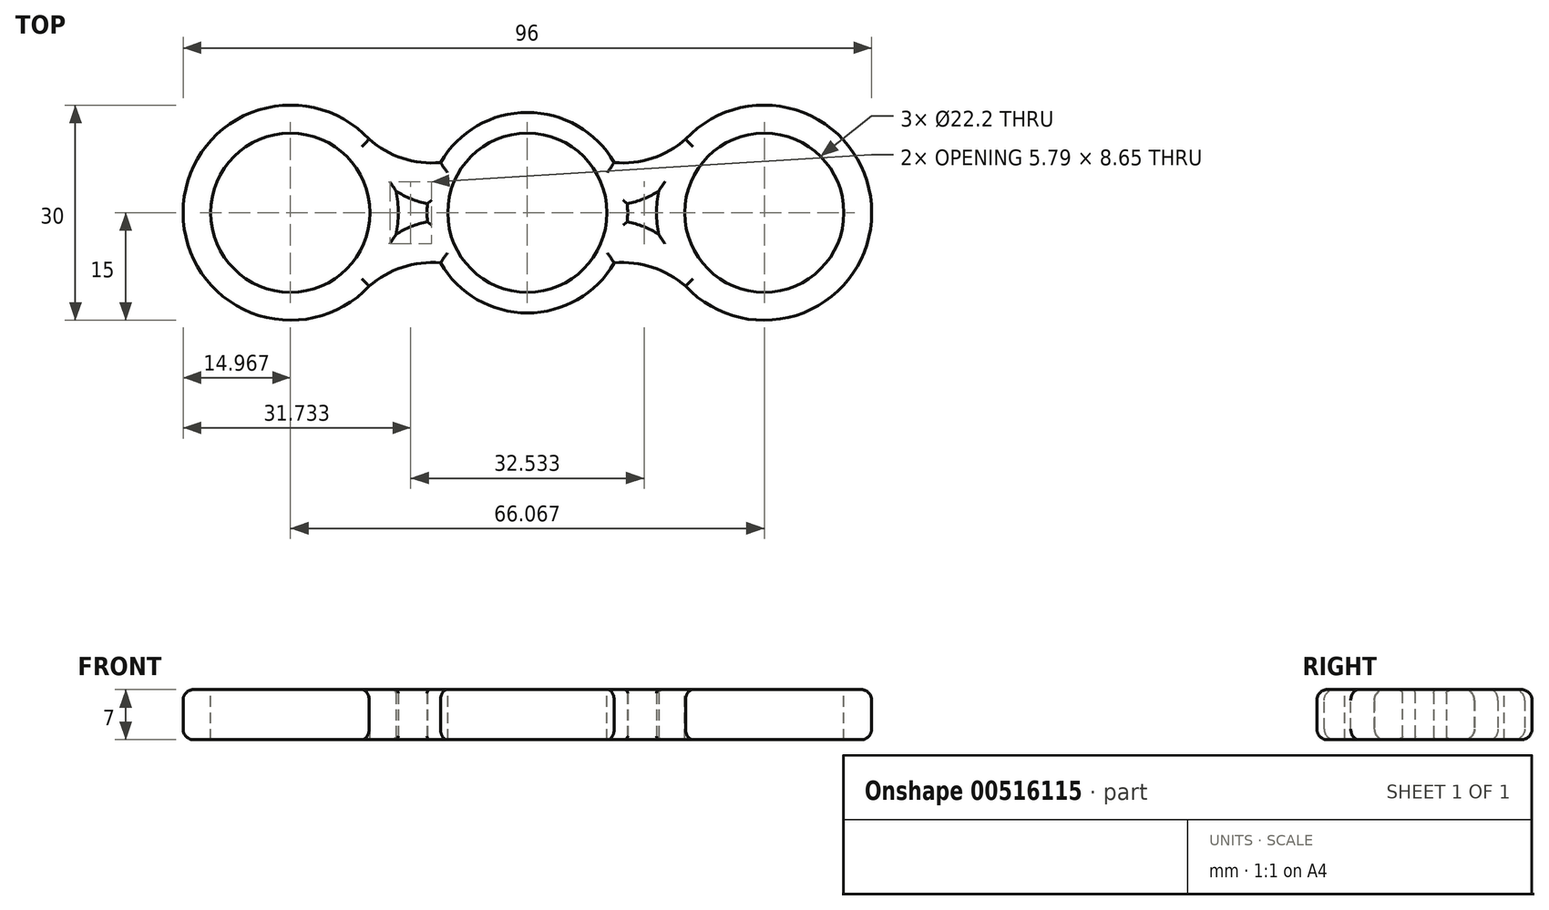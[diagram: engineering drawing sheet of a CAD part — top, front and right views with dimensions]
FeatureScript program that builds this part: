
annotation { "Feature Type Name" : "Feature", "Feature Type Description" : "" }
export const myFeature = defineFeature(function(context is Context, id is Id, definition is map)
    precondition{}
    {
        {
            var Q0;
            Q0=qCreatedBy(makeId("Top.planeOp"),FACE);
            var sketch = newSketch(context, id + "F0", { "sketchPlane" : qUnion([Q0])});
            skLineSegment(sketch, "E0", {"start": v(0, 0) * mm, "end": v(-13.98, 0) * mm});
            skLineSegment(sketch, "E1", {"start": v(0, 0) * mm, "end": v(0, 14) * mm});
            skArc(sketch, "E2", {"start": v(0, 13.98) * mm, "mid": v(-9.89, 9.89) * mm, "end": v(-13.98, 0) * mm});
            skArc(sketch, "E3", {"start": v(-18, 0) * mm, "mid": v(-33, 15) * mm, "end": v(-48, 0) * mm});
            skArc(sketch, "E4", {"start": v(-23, 11.18) * mm, "mid": v(-18.04, 7.82) * mm, "end": v(-12.1, 7) * mm});
            skArc(sketch, "E5", {"start": v(-18.31, 3.04) * mm, "mid": v(-16.2, 1.93) * mm, "end": v(-13.92, 1.28) * mm});
            skLineSegment(sketch, "E6.trimOffspring", {"start": v(-18, 0) * mm, "end": v(-48, 0) * mm});
            skSolve(sketch);
        }
        {
            var Q0;
            Q0 = qSketchRegion(id + "F0", true);
            extrude(context, id + "F1", {"entities" : qUnion([Q0]), "depth" : 7 * mm, "offsetDistance" : 25 * mm});
        }
        {
            var Q0;
            Q0=qCreatedBy(makeId("Top.planeOp"),FACE);
            cPlane(context, id + "F2", {"entities" : qUnion([Q0]), "cplaneType" : CPlaneType.OFFSET, "offset" : 7 * mm, "width" : 150 * mm, "height" : 150 * mm});
        }
        {
            var Q0;
            Q0=qCreatedBy(id+"F2.planeOp",FACE);
            var sketch = newSketch(context, id + "F3", { "sketchPlane" : qUnion([Q0])});
            skCircle(sketch, "E7", {"center": v(-33.03, 0) * mm, "radius": 11.1 * mm});
            skCircle(sketch, "E8", {"center": v(0, 0) * mm, "radius": 11.1 * mm});
            skSolve(sketch);
        }
        {
            var Q0;
            Q0 = qSketchRegion(id + "F3", true);
            extrude(context, id + "F4", {"entities" : qUnion([Q0]), "operationType" : NewBodyOperationType.REMOVE, "oppositeDirection" : true, "depth" : 25 * mm, "offsetDistance" : 25 * mm});
        }
        {
            var Q0;
            Q0=makeQuery(id+"F1.opExtrude","SWEPT_BODY",BODY,{"disambiguationData":[OSD([sQuery(id+"F0.wireOp",EDGE,"E0"),sQuery(id+"F0.wireOp",EDGE,"E1"),sQuery(id+"F0.wireOp",EDGE,"E2"),sQuery(id+"F0.wireOp",EDGE,"E3"),sQuery(id+"F0.wireOp",EDGE,"E4"),sQuery(id+"F0.wireOp",EDGE,"E5"),sQuery(id+"F0.wireOp",EDGE,"E6.trimOffspring")])]});
            transform(context, id + "F5", {"entities" : qUnion([Q0]), "transformType" : TransformType.TRANSLATION_3D, "dx" : 53.6 * mm, "dy" : 0.3 * mm, "dz" : 0 * mm, "makeCopy" : true});
        }
        {
            var Q0;
            Q0=makeQuery(id+"F1.opExtrude","SWEPT_BODY",BODY,{"disambiguationData":[OSD([sQuery(id+"F0.wireOp",EDGE,"E0"),sQuery(id+"F0.wireOp",EDGE,"E1"),sQuery(id+"F0.wireOp",EDGE,"E2"),sQuery(id+"F0.wireOp",EDGE,"E3"),sQuery(id+"F0.wireOp",EDGE,"E4"),sQuery(id+"F0.wireOp",EDGE,"E5"),sQuery(id+"F0.wireOp",EDGE,"E6.trimOffspring")])]});
            var Q1;
            Q1=sQuery(id+"F0.wireOp",EDGE,"E6.trimOffspring");
            transform(context, id + "F6", {"entities" : qUnion([Q0]), "transformType" : TransformType.ROTATION, "transformAxis" : qUnion([Q1]), "angle" : 180 * degree, "makeCopy" : true});
        }
        {
            var Q0;
            Q0=makeQuery(id+"F5.opPattern","COPY",BODY,{"derivedFrom":makeQuery(id+"F1.opExtrude","SWEPT_BODY",BODY,{"disambiguationData":[OSD([sQuery(id+"F0.wireOp",EDGE,"E0"),sQuery(id+"F0.wireOp",EDGE,"E1"),sQuery(id+"F0.wireOp",EDGE,"E2"),sQuery(id+"F0.wireOp",EDGE,"E3"),sQuery(id+"F0.wireOp",EDGE,"E4"),sQuery(id+"F0.wireOp",EDGE,"E5"),sQuery(id+"F0.wireOp",EDGE,"E6.trimOffspring")])]}),"instanceName":"1"});
            deleteBodies(context, id + "F7", {"entities" : qUnion([Q0])});
        }
        {
            var Q0;
            Q0=makeQuery(id+"F6.opPattern","COPY",BODY,{"derivedFrom":makeQuery(id+"F1.opExtrude","SWEPT_BODY",BODY,{"disambiguationData":[OSD([sQuery(id+"F0.wireOp",EDGE,"E0"),sQuery(id+"F0.wireOp",EDGE,"E1"),sQuery(id+"F0.wireOp",EDGE,"E2"),sQuery(id+"F0.wireOp",EDGE,"E3"),sQuery(id+"F0.wireOp",EDGE,"E4"),sQuery(id+"F0.wireOp",EDGE,"E5"),sQuery(id+"F0.wireOp",EDGE,"E6.trimOffspring")])]}),"instanceName":"1"});
            var Q1;
            Q1=qCreatedBy(id+"F2.planeOp",FACE);
            transform(context, id + "F8", {"entities" : qUnion([Q0]), "transformType" : TransformType.TRANSLATION_DISTANCE, "transformDirection" : qUnion([Q1]), "distance" : 7 * mm, "makeCopy" : false});
        }
        {
            var Q0;
            Q0=makeQuery(id+"F1.opExtrude","SWEPT_BODY",BODY,{"disambiguationData":[OSD([sQuery(id+"F0.wireOp",EDGE,"E0"),sQuery(id+"F0.wireOp",EDGE,"E1"),sQuery(id+"F0.wireOp",EDGE,"E2"),sQuery(id+"F0.wireOp",EDGE,"E3"),sQuery(id+"F0.wireOp",EDGE,"E4"),sQuery(id+"F0.wireOp",EDGE,"E5"),sQuery(id+"F0.wireOp",EDGE,"E6.trimOffspring")])]});
            var Q1;
            Q1=makeQuery(id+"F6.opPattern","COPY",BODY,{"derivedFrom":makeQuery(id+"F1.opExtrude","SWEPT_BODY",BODY,{"disambiguationData":[OSD([sQuery(id+"F0.wireOp",EDGE,"E0"),sQuery(id+"F0.wireOp",EDGE,"E1"),sQuery(id+"F0.wireOp",EDGE,"E2"),sQuery(id+"F0.wireOp",EDGE,"E3"),sQuery(id+"F0.wireOp",EDGE,"E4"),sQuery(id+"F0.wireOp",EDGE,"E5"),sQuery(id+"F0.wireOp",EDGE,"E6.trimOffspring")])]}),"instanceName":"1"});
            var Q2;
            Q2=sQuery(id+"F0.wireOp",EDGE,"E1");
            transform(context, id + "F9", {"entities" : qUnion([Q0, Q1]), "transformType" : TransformType.ROTATION, "transformAxis" : qUnion([Q2]), "angle" : 180 * degree, "makeCopy" : true});
        }
        {
            var Q0;
            Q0=makeQuery(id+"F9.opPattern","COPY",BODY,{"derivedFrom":makeQuery(id+"F1.opExtrude","SWEPT_BODY",BODY,{"disambiguationData":[OSD([sQuery(id+"F0.wireOp",EDGE,"E0"),sQuery(id+"F0.wireOp",EDGE,"E1"),sQuery(id+"F0.wireOp",EDGE,"E2"),sQuery(id+"F0.wireOp",EDGE,"E3"),sQuery(id+"F0.wireOp",EDGE,"E4"),sQuery(id+"F0.wireOp",EDGE,"E5"),sQuery(id+"F0.wireOp",EDGE,"E6.trimOffspring")])]}),"instanceName":"1"});
            var Q1;
            Q1=makeQuery(id+"F9.opPattern","COPY",BODY,{"derivedFrom":makeQuery(id+"F6.opPattern","COPY",BODY,{"derivedFrom":makeQuery(id+"F1.opExtrude","SWEPT_BODY",BODY,{"disambiguationData":[OSD([sQuery(id+"F0.wireOp",EDGE,"E0"),sQuery(id+"F0.wireOp",EDGE,"E1"),sQuery(id+"F0.wireOp",EDGE,"E2"),sQuery(id+"F0.wireOp",EDGE,"E3"),sQuery(id+"F0.wireOp",EDGE,"E4"),sQuery(id+"F0.wireOp",EDGE,"E5"),sQuery(id+"F0.wireOp",EDGE,"E6.trimOffspring")])]}),"instanceName":"1"}),"instanceName":"1"});
            var Q2;
            Q2=qCreatedBy(id+"F2.planeOp",FACE);
            transform(context, id + "F10", {"entities" : qUnion([Q0, Q1]), "transformType" : TransformType.TRANSLATION_DISTANCE, "transformDirection" : qUnion([Q2]), "distance" : 7 * mm, "makeCopy" : false});
        }
        {
            var Q0;
            Q0=makeQuery(id+"F1.opExtrude","SWEPT_BODY",BODY,{"disambiguationData":[OSD([sQuery(id+"F0.wireOp",EDGE,"E0"),sQuery(id+"F0.wireOp",EDGE,"E1"),sQuery(id+"F0.wireOp",EDGE,"E2"),sQuery(id+"F0.wireOp",EDGE,"E3"),sQuery(id+"F0.wireOp",EDGE,"E4"),sQuery(id+"F0.wireOp",EDGE,"E5"),sQuery(id+"F0.wireOp",EDGE,"E6.trimOffspring")])]});
            var Q1;
            Q1=makeQuery(id+"F6.opPattern","COPY",BODY,{"derivedFrom":makeQuery(id+"F1.opExtrude","SWEPT_BODY",BODY,{"disambiguationData":[OSD([sQuery(id+"F0.wireOp",EDGE,"E0"),sQuery(id+"F0.wireOp",EDGE,"E1"),sQuery(id+"F0.wireOp",EDGE,"E2"),sQuery(id+"F0.wireOp",EDGE,"E3"),sQuery(id+"F0.wireOp",EDGE,"E4"),sQuery(id+"F0.wireOp",EDGE,"E5"),sQuery(id+"F0.wireOp",EDGE,"E6.trimOffspring")])]}),"instanceName":"1"});
            var Q2;
            Q2=makeQuery(id+"F9.opPattern","COPY",BODY,{"derivedFrom":makeQuery(id+"F6.opPattern","COPY",BODY,{"derivedFrom":makeQuery(id+"F1.opExtrude","SWEPT_BODY",BODY,{"disambiguationData":[OSD([sQuery(id+"F0.wireOp",EDGE,"E0"),sQuery(id+"F0.wireOp",EDGE,"E1"),sQuery(id+"F0.wireOp",EDGE,"E2"),sQuery(id+"F0.wireOp",EDGE,"E3"),sQuery(id+"F0.wireOp",EDGE,"E4"),sQuery(id+"F0.wireOp",EDGE,"E5"),sQuery(id+"F0.wireOp",EDGE,"E6.trimOffspring")])]}),"instanceName":"1"}),"instanceName":"1"});
            var Q3;
            Q3=makeQuery(id+"F9.opPattern","COPY",BODY,{"derivedFrom":makeQuery(id+"F1.opExtrude","SWEPT_BODY",BODY,{"disambiguationData":[OSD([sQuery(id+"F0.wireOp",EDGE,"E0"),sQuery(id+"F0.wireOp",EDGE,"E1"),sQuery(id+"F0.wireOp",EDGE,"E2"),sQuery(id+"F0.wireOp",EDGE,"E3"),sQuery(id+"F0.wireOp",EDGE,"E4"),sQuery(id+"F0.wireOp",EDGE,"E5"),sQuery(id+"F0.wireOp",EDGE,"E6.trimOffspring")])]}),"instanceName":"1"});
            booleanBodies(context, id + "F11", {"operationType" : BooleanOperationType.UNION, "tools" : qUnion([Q0, Q1, Q2, Q3])});
        }
        {
            var Q0;
            {var subQ0=sQuery(id+"F0.wireOp",EDGE,"E3");var subQ1=sQuery(id+"F0.wireOp",EDGE,"E4");var subQ2=makeQuery(id+"F0.imprint","INTERSECT",VERTEX,{"disambiguationData":[OD(0.0)],"derivedFrom":[subQ0,subQ1]});var subQ3=makeQuery(id+"F0.imprint","IMPRINT",EDGE,{"disambiguationData":[TD([[makeQuery(id+"F0.imprint","INTERSECT",VERTEX,{"disambiguationData":[OD(1.0)],"derivedFrom":[subQ0,sQuery(id+"F0.wireOp",EDGE,"E6.trimOffspring")]}),1.0]])],"derivedFrom":subQ0});var subQ4=makeQuery(id+"F0.imprint","IMPRINT",EDGE,{"disambiguationData":[TD([[subQ2,1.0]])],"derivedFrom":subQ0});Q0=makeQuery(id+"F11.opBoolean","MERGE",EDGE,{"derivedFrom":[makeQuery(id+"F9.opPattern","COPY",EDGE,{"derivedFrom":makeQuery(id+"F1.opExtrude","CAP_EDGE",EDGE,{"disambiguationData":[OSD([subQ0]),TDD([subQ4,subQ3])],"isStart":false}),"instanceName":"1"}),makeQuery(id+"F9.opPattern","COPY",EDGE,{"derivedFrom":makeQuery(id+"F6.opPattern","COPY",EDGE,{"derivedFrom":makeQuery(id+"F1.opExtrude","CAP_EDGE",EDGE,{"disambiguationData":[OSD([subQ0]),TDD([subQ4,subQ3])],"isStart":true}),"instanceName":"1"}),"instanceName":"1"})]});}
            var Q1;
            Q1=makeQuery(id+"F9.opPattern","COPY",EDGE,{"derivedFrom":makeQuery(id+"F1.opExtrude","CAP_EDGE",EDGE,{"disambiguationData":[OSD([sQuery(id+"F0.wireOp",EDGE,"E4")])],"isStart":false}),"instanceName":"1"});
            var Q2;
            Q2=makeQuery(id+"F9.opPattern","COPY",EDGE,{"derivedFrom":makeQuery(id+"F6.opPattern","COPY",EDGE,{"derivedFrom":makeQuery(id+"F1.opExtrude","CAP_EDGE",EDGE,{"disambiguationData":[OSD([sQuery(id+"F0.wireOp",EDGE,"E4")])],"isStart":true}),"instanceName":"1"}),"instanceName":"1"});
            var Q3;
            {var subQ0=sQuery(id+"F0.wireOp",EDGE,"E2");var subQ1=makeQuery(id+"F0.imprint","IMPRINT",EDGE,{"disambiguationData":[TD([[makeQuery(id+"F0.imprint","INTERSECT",VERTEX,{"derivedFrom":[sQuery(id+"F0.wireOp",EDGE,"E1"),subQ0]}),-1.0]])],"derivedFrom":subQ0});Q3=makeQuery(id+"F11.opBoolean","MERGE",EDGE,{"derivedFrom":[makeQuery(id+"F6.opPattern","COPY",EDGE,{"derivedFrom":makeQuery(id+"F1.opExtrude","CAP_EDGE",EDGE,{"disambiguationData":[OSD([subQ0]),TDD([subQ1])],"isStart":false}),"instanceName":"1"}),makeQuery(id+"F9.opPattern","COPY",EDGE,{"derivedFrom":makeQuery(id+"F6.opPattern","COPY",EDGE,{"derivedFrom":makeQuery(id+"F1.opExtrude","CAP_EDGE",EDGE,{"disambiguationData":[OSD([subQ0]),TDD([subQ1])],"isStart":true}),"instanceName":"1"}),"instanceName":"1"})]});}
            var Q4;
            {var subQ0=sQuery(id+"F0.wireOp",EDGE,"E2");var subQ1=makeQuery(id+"F0.imprint","IMPRINT",EDGE,{"disambiguationData":[TD([[makeQuery(id+"F0.imprint","INTERSECT",VERTEX,{"derivedFrom":[sQuery(id+"F0.wireOp",EDGE,"E1"),subQ0]}),-1.0]])],"derivedFrom":subQ0});Q4=makeQuery(id+"F11.opBoolean","MERGE",EDGE,{"derivedFrom":[makeQuery(id+"F1.opExtrude","CAP_EDGE",EDGE,{"disambiguationData":[OSD([subQ0]),TDD([subQ1])],"isStart":true}),makeQuery(id+"F9.opPattern","COPY",EDGE,{"derivedFrom":makeQuery(id+"F1.opExtrude","CAP_EDGE",EDGE,{"disambiguationData":[OSD([subQ0]),TDD([subQ1])],"isStart":false}),"instanceName":"1"})]});}
            var Q5;
            Q5=makeQuery(id+"F1.opExtrude","CAP_EDGE",EDGE,{"disambiguationData":[OSD([sQuery(id+"F0.wireOp",EDGE,"E4")])],"isStart":true});
            var Q6;
            {var subQ0=sQuery(id+"F0.wireOp",EDGE,"E3");var subQ1=sQuery(id+"F0.wireOp",EDGE,"E4");var subQ2=makeQuery(id+"F0.imprint","INTERSECT",VERTEX,{"disambiguationData":[OD(0.0)],"derivedFrom":[subQ0,subQ1]});var subQ3=makeQuery(id+"F0.imprint","IMPRINT",EDGE,{"disambiguationData":[TD([[makeQuery(id+"F0.imprint","INTERSECT",VERTEX,{"disambiguationData":[OD(1.0)],"derivedFrom":[subQ0,sQuery(id+"F0.wireOp",EDGE,"E6.trimOffspring")]}),1.0]])],"derivedFrom":subQ0});var subQ4=makeQuery(id+"F0.imprint","IMPRINT",EDGE,{"disambiguationData":[TD([[subQ2,1.0]])],"derivedFrom":subQ0});Q6=makeQuery(id+"F11.opBoolean","MERGE",EDGE,{"derivedFrom":[makeQuery(id+"F1.opExtrude","CAP_EDGE",EDGE,{"disambiguationData":[OSD([subQ0]),TDD([subQ4,subQ3])],"isStart":true}),makeQuery(id+"F6.opPattern","COPY",EDGE,{"derivedFrom":makeQuery(id+"F1.opExtrude","CAP_EDGE",EDGE,{"disambiguationData":[OSD([subQ0]),TDD([subQ4,subQ3])],"isStart":false}),"instanceName":"1"})]});}
            var Q7;
            Q7=makeQuery(id+"F6.opPattern","COPY",EDGE,{"derivedFrom":makeQuery(id+"F1.opExtrude","CAP_EDGE",EDGE,{"disambiguationData":[OSD([sQuery(id+"F0.wireOp",EDGE,"E4")])],"isStart":false}),"instanceName":"1"});
            fillet(context, id + "F12", {"entities" : qUnion([Q0, Q1, Q2, Q3, Q4, Q5, Q6, Q7]), "radius" : 1.5 * mm, "tangentPropagation" : true, "allowEdgeOverflow" : false});
        }
        {
            var Q0;
            {var subQ0=sQuery(id+"F0.wireOp",EDGE,"E3");var subQ1=sQuery(id+"F0.wireOp",EDGE,"E4");var subQ2=makeQuery(id+"F0.imprint","INTERSECT",VERTEX,{"disambiguationData":[OD(0.0)],"derivedFrom":[subQ0,subQ1]});var subQ3=makeQuery(id+"F0.imprint","IMPRINT",EDGE,{"disambiguationData":[TD([[makeQuery(id+"F0.imprint","INTERSECT",VERTEX,{"disambiguationData":[OD(1.0)],"derivedFrom":[subQ0,sQuery(id+"F0.wireOp",EDGE,"E6.trimOffspring")]}),1.0]])],"derivedFrom":subQ0});var subQ4=makeQuery(id+"F0.imprint","IMPRINT",EDGE,{"disambiguationData":[TD([[subQ2,1.0]])],"derivedFrom":subQ0});Q0=makeQuery(id+"F11.opBoolean","MERGE",EDGE,{"derivedFrom":[makeQuery(id+"F1.opExtrude","CAP_EDGE",EDGE,{"disambiguationData":[OSD([subQ0]),TDD([subQ4,subQ3])],"isStart":false}),makeQuery(id+"F6.opPattern","COPY",EDGE,{"derivedFrom":makeQuery(id+"F1.opExtrude","CAP_EDGE",EDGE,{"disambiguationData":[OSD([subQ0]),TDD([subQ4,subQ3])],"isStart":true}),"instanceName":"1"})]});}
            var Q1;
            Q1=makeQuery(id+"F1.opExtrude","CAP_EDGE",EDGE,{"disambiguationData":[OSD([sQuery(id+"F0.wireOp",EDGE,"E4")])],"isStart":false});
            var Q2;
            Q2=makeQuery(id+"F6.opPattern","COPY",EDGE,{"derivedFrom":makeQuery(id+"F1.opExtrude","CAP_EDGE",EDGE,{"disambiguationData":[OSD([sQuery(id+"F0.wireOp",EDGE,"E4")])],"isStart":true}),"instanceName":"1"});
            var Q3;
            {var subQ0=sQuery(id+"F0.wireOp",EDGE,"E2");var subQ1=makeQuery(id+"F0.imprint","IMPRINT",EDGE,{"disambiguationData":[TD([[makeQuery(id+"F0.imprint","INTERSECT",VERTEX,{"derivedFrom":[sQuery(id+"F0.wireOp",EDGE,"E1"),subQ0]}),-1.0]])],"derivedFrom":subQ0});Q3=makeQuery(id+"F11.opBoolean","MERGE",EDGE,{"derivedFrom":[makeQuery(id+"F6.opPattern","COPY",EDGE,{"derivedFrom":makeQuery(id+"F1.opExtrude","CAP_EDGE",EDGE,{"disambiguationData":[OSD([subQ0]),TDD([subQ1])],"isStart":true}),"instanceName":"1"}),makeQuery(id+"F9.opPattern","COPY",EDGE,{"derivedFrom":makeQuery(id+"F6.opPattern","COPY",EDGE,{"derivedFrom":makeQuery(id+"F1.opExtrude","CAP_EDGE",EDGE,{"disambiguationData":[OSD([subQ0]),TDD([subQ1])],"isStart":false}),"instanceName":"1"}),"instanceName":"1"})]});}
            var Q4;
            {var subQ0=sQuery(id+"F0.wireOp",EDGE,"E2");var subQ1=makeQuery(id+"F0.imprint","IMPRINT",EDGE,{"disambiguationData":[TD([[makeQuery(id+"F0.imprint","INTERSECT",VERTEX,{"derivedFrom":[sQuery(id+"F0.wireOp",EDGE,"E1"),subQ0]}),-1.0]])],"derivedFrom":subQ0});Q4=makeQuery(id+"F11.opBoolean","MERGE",EDGE,{"derivedFrom":[makeQuery(id+"F1.opExtrude","CAP_EDGE",EDGE,{"disambiguationData":[OSD([subQ0]),TDD([subQ1])],"isStart":false}),makeQuery(id+"F9.opPattern","COPY",EDGE,{"derivedFrom":makeQuery(id+"F1.opExtrude","CAP_EDGE",EDGE,{"disambiguationData":[OSD([subQ0]),TDD([subQ1])],"isStart":true}),"instanceName":"1"})]});}
            var Q5;
            Q5=makeQuery(id+"F9.opPattern","COPY",EDGE,{"derivedFrom":makeQuery(id+"F1.opExtrude","CAP_EDGE",EDGE,{"disambiguationData":[OSD([sQuery(id+"F0.wireOp",EDGE,"E4")])],"isStart":true}),"instanceName":"1"});
            var Q6;
            {var subQ0=sQuery(id+"F0.wireOp",EDGE,"E3");var subQ1=sQuery(id+"F0.wireOp",EDGE,"E4");var subQ2=makeQuery(id+"F0.imprint","INTERSECT",VERTEX,{"disambiguationData":[OD(0.0)],"derivedFrom":[subQ0,subQ1]});var subQ3=makeQuery(id+"F0.imprint","IMPRINT",EDGE,{"disambiguationData":[TD([[makeQuery(id+"F0.imprint","INTERSECT",VERTEX,{"disambiguationData":[OD(1.0)],"derivedFrom":[subQ0,sQuery(id+"F0.wireOp",EDGE,"E6.trimOffspring")]}),1.0]])],"derivedFrom":subQ0});var subQ4=makeQuery(id+"F0.imprint","IMPRINT",EDGE,{"disambiguationData":[TD([[subQ2,1.0]])],"derivedFrom":subQ0});Q6=makeQuery(id+"F11.opBoolean","MERGE",EDGE,{"derivedFrom":[makeQuery(id+"F9.opPattern","COPY",EDGE,{"derivedFrom":makeQuery(id+"F1.opExtrude","CAP_EDGE",EDGE,{"disambiguationData":[OSD([subQ0]),TDD([subQ4,subQ3])],"isStart":true}),"instanceName":"1"}),makeQuery(id+"F9.opPattern","COPY",EDGE,{"derivedFrom":makeQuery(id+"F6.opPattern","COPY",EDGE,{"derivedFrom":makeQuery(id+"F1.opExtrude","CAP_EDGE",EDGE,{"disambiguationData":[OSD([subQ0]),TDD([subQ4,subQ3])],"isStart":false}),"instanceName":"1"}),"instanceName":"1"})]});}
            var Q7;
            Q7=makeQuery(id+"F9.opPattern","COPY",EDGE,{"derivedFrom":makeQuery(id+"F6.opPattern","COPY",EDGE,{"derivedFrom":makeQuery(id+"F1.opExtrude","CAP_EDGE",EDGE,{"disambiguationData":[OSD([sQuery(id+"F0.wireOp",EDGE,"E4")])],"isStart":false}),"instanceName":"1"}),"instanceName":"1"});
            fillet(context, id + "F13", {"entities" : qUnion([Q0, Q1, Q2, Q3, Q4, Q5, Q6, Q7]), "radius" : 1.5 * mm, "tangentPropagation" : true, "allowEdgeOverflow" : false});
        }
        {
            var Q0;
            Q0=makeQuery(id+"F9.opPattern","COPY",EDGE,{"derivedFrom":makeQuery(id+"F1.opExtrude","CAP_EDGE",EDGE,{"disambiguationData":[OSD([sQuery(id+"F0.wireOp",EDGE,"E5")])],"isStart":false}),"instanceName":"1"});
            var Q1;
            Q1=makeQuery(id+"F1.opExtrude","CAP_EDGE",EDGE,{"disambiguationData":[OSD([sQuery(id+"F0.wireOp",EDGE,"E5")])],"isStart":true});
            var Q2;
            {var subQ0=sQuery(id+"F0.wireOp",EDGE,"E3");var subQ1=makeQuery(id+"F0.imprint","IMPRINT",EDGE,{"disambiguationData":[TD([[makeQuery(id+"F0.imprint","INTERSECT",VERTEX,{"disambiguationData":[OD(0.0)],"derivedFrom":[subQ0,sQuery(id+"F0.wireOp",EDGE,"E6.trimOffspring")]}),-1.0]])],"derivedFrom":subQ0});Q2=makeQuery(id+"F11.opBoolean","MERGE",EDGE,{"derivedFrom":[makeQuery(id+"F1.opExtrude","CAP_EDGE",EDGE,{"disambiguationData":[OSD([subQ0]),TDD([subQ1])],"isStart":true}),makeQuery(id+"F6.opPattern","COPY",EDGE,{"derivedFrom":makeQuery(id+"F1.opExtrude","CAP_EDGE",EDGE,{"disambiguationData":[OSD([subQ0]),TDD([subQ1])],"isStart":false}),"instanceName":"1"})]});}
            var Q3;
            Q3=makeQuery(id+"F6.opPattern","COPY",EDGE,{"derivedFrom":makeQuery(id+"F1.opExtrude","CAP_EDGE",EDGE,{"disambiguationData":[OSD([sQuery(id+"F0.wireOp",EDGE,"E5")])],"isStart":false}),"instanceName":"1"});
            var Q4;
            {var subQ0=sQuery(id+"F0.wireOp",EDGE,"E3");var subQ1=makeQuery(id+"F0.imprint","IMPRINT",EDGE,{"disambiguationData":[TD([[makeQuery(id+"F0.imprint","INTERSECT",VERTEX,{"disambiguationData":[OD(0.0)],"derivedFrom":[subQ0,sQuery(id+"F0.wireOp",EDGE,"E6.trimOffspring")]}),-1.0]])],"derivedFrom":subQ0});Q4=makeQuery(id+"F11.opBoolean","MERGE",EDGE,{"derivedFrom":[makeQuery(id+"F1.opExtrude","CAP_EDGE",EDGE,{"disambiguationData":[OSD([subQ0]),TDD([subQ1])],"isStart":false}),makeQuery(id+"F6.opPattern","COPY",EDGE,{"derivedFrom":makeQuery(id+"F1.opExtrude","CAP_EDGE",EDGE,{"disambiguationData":[OSD([subQ0]),TDD([subQ1])],"isStart":true}),"instanceName":"1"})]});}
            var Q5;
            Q5=makeQuery(id+"F1.opExtrude","CAP_EDGE",EDGE,{"disambiguationData":[OSD([sQuery(id+"F0.wireOp",EDGE,"E5")])],"isStart":false});
            var Q6;
            {var subQ0=sQuery(id+"F0.wireOp",EDGE,"E2");var subQ1=makeQuery(id+"F0.imprint","IMPRINT",EDGE,{"disambiguationData":[TD([[makeQuery(id+"F0.imprint","INTERSECT",VERTEX,{"derivedFrom":[sQuery(id+"F0.wireOp",EDGE,"E0"),subQ0]}),1.0]])],"derivedFrom":subQ0});Q6=makeQuery(id+"F11.opBoolean","MERGE",EDGE,{"derivedFrom":[makeQuery(id+"F1.opExtrude","CAP_EDGE",EDGE,{"disambiguationData":[OSD([subQ0]),TDD([subQ1])],"isStart":false}),makeQuery(id+"F6.opPattern","COPY",EDGE,{"derivedFrom":makeQuery(id+"F1.opExtrude","CAP_EDGE",EDGE,{"disambiguationData":[OSD([subQ0]),TDD([subQ1])],"isStart":true}),"instanceName":"1"})]});}
            var Q7;
            Q7=makeQuery(id+"F6.opPattern","COPY",EDGE,{"derivedFrom":makeQuery(id+"F1.opExtrude","CAP_EDGE",EDGE,{"disambiguationData":[OSD([sQuery(id+"F0.wireOp",EDGE,"E5")])],"isStart":true}),"instanceName":"1"});
            var Q8;
            {var subQ0=sQuery(id+"F0.wireOp",EDGE,"E2");var subQ1=makeQuery(id+"F0.imprint","IMPRINT",EDGE,{"disambiguationData":[TD([[makeQuery(id+"F0.imprint","INTERSECT",VERTEX,{"derivedFrom":[sQuery(id+"F0.wireOp",EDGE,"E0"),subQ0]}),1.0]])],"derivedFrom":subQ0});Q8=makeQuery(id+"F11.opBoolean","MERGE",EDGE,{"derivedFrom":[makeQuery(id+"F1.opExtrude","CAP_EDGE",EDGE,{"disambiguationData":[OSD([subQ0]),TDD([subQ1])],"isStart":true}),makeQuery(id+"F6.opPattern","COPY",EDGE,{"derivedFrom":makeQuery(id+"F1.opExtrude","CAP_EDGE",EDGE,{"disambiguationData":[OSD([subQ0]),TDD([subQ1])],"isStart":false}),"instanceName":"1"})]});}
            var Q9;
            {var subQ0=sQuery(id+"F0.wireOp",EDGE,"E2");var subQ1=makeQuery(id+"F0.imprint","IMPRINT",EDGE,{"disambiguationData":[TD([[makeQuery(id+"F0.imprint","INTERSECT",VERTEX,{"derivedFrom":[sQuery(id+"F0.wireOp",EDGE,"E0"),subQ0]}),1.0]])],"derivedFrom":subQ0});Q9=makeQuery(id+"F11.opBoolean","MERGE",EDGE,{"derivedFrom":[makeQuery(id+"F9.opPattern","COPY",EDGE,{"derivedFrom":makeQuery(id+"F1.opExtrude","CAP_EDGE",EDGE,{"disambiguationData":[OSD([subQ0]),TDD([subQ1])],"isStart":false}),"instanceName":"1"}),makeQuery(id+"F9.opPattern","COPY",EDGE,{"derivedFrom":makeQuery(id+"F6.opPattern","COPY",EDGE,{"derivedFrom":makeQuery(id+"F1.opExtrude","CAP_EDGE",EDGE,{"disambiguationData":[OSD([subQ0]),TDD([subQ1])],"isStart":true}),"instanceName":"1"}),"instanceName":"1"})]});}
            var Q10;
            {var subQ0=sQuery(id+"F0.wireOp",EDGE,"E3");var subQ1=makeQuery(id+"F0.imprint","IMPRINT",EDGE,{"disambiguationData":[TD([[makeQuery(id+"F0.imprint","INTERSECT",VERTEX,{"disambiguationData":[OD(0.0)],"derivedFrom":[subQ0,sQuery(id+"F0.wireOp",EDGE,"E6.trimOffspring")]}),-1.0]])],"derivedFrom":subQ0});Q10=makeQuery(id+"F11.opBoolean","MERGE",EDGE,{"derivedFrom":[makeQuery(id+"F9.opPattern","COPY",EDGE,{"derivedFrom":makeQuery(id+"F1.opExtrude","CAP_EDGE",EDGE,{"disambiguationData":[OSD([subQ0]),TDD([subQ1])],"isStart":false}),"instanceName":"1"}),makeQuery(id+"F9.opPattern","COPY",EDGE,{"derivedFrom":makeQuery(id+"F6.opPattern","COPY",EDGE,{"derivedFrom":makeQuery(id+"F1.opExtrude","CAP_EDGE",EDGE,{"disambiguationData":[OSD([subQ0]),TDD([subQ1])],"isStart":true}),"instanceName":"1"}),"instanceName":"1"})]});}
            var Q11;
            Q11=makeQuery(id+"F9.opPattern","COPY",EDGE,{"derivedFrom":makeQuery(id+"F6.opPattern","COPY",EDGE,{"derivedFrom":makeQuery(id+"F1.opExtrude","CAP_EDGE",EDGE,{"disambiguationData":[OSD([sQuery(id+"F0.wireOp",EDGE,"E5")])],"isStart":true}),"instanceName":"1"}),"instanceName":"1"});
            var Q12;
            Q12=makeQuery(id+"F9.opPattern","COPY",EDGE,{"derivedFrom":makeQuery(id+"F1.opExtrude","CAP_EDGE",EDGE,{"disambiguationData":[OSD([sQuery(id+"F0.wireOp",EDGE,"E5")])],"isStart":true}),"instanceName":"1"});
            var Q13;
            {var subQ0=sQuery(id+"F0.wireOp",EDGE,"E3");var subQ1=makeQuery(id+"F0.imprint","IMPRINT",EDGE,{"disambiguationData":[TD([[makeQuery(id+"F0.imprint","INTERSECT",VERTEX,{"disambiguationData":[OD(0.0)],"derivedFrom":[subQ0,sQuery(id+"F0.wireOp",EDGE,"E6.trimOffspring")]}),-1.0]])],"derivedFrom":subQ0});Q13=makeQuery(id+"F11.opBoolean","MERGE",EDGE,{"derivedFrom":[makeQuery(id+"F9.opPattern","COPY",EDGE,{"derivedFrom":makeQuery(id+"F1.opExtrude","CAP_EDGE",EDGE,{"disambiguationData":[OSD([subQ0]),TDD([subQ1])],"isStart":true}),"instanceName":"1"}),makeQuery(id+"F9.opPattern","COPY",EDGE,{"derivedFrom":makeQuery(id+"F6.opPattern","COPY",EDGE,{"derivedFrom":makeQuery(id+"F1.opExtrude","CAP_EDGE",EDGE,{"disambiguationData":[OSD([subQ0]),TDD([subQ1])],"isStart":false}),"instanceName":"1"}),"instanceName":"1"})]});}
            var Q14;
            Q14=makeQuery(id+"F9.opPattern","COPY",EDGE,{"derivedFrom":makeQuery(id+"F6.opPattern","COPY",EDGE,{"derivedFrom":makeQuery(id+"F1.opExtrude","CAP_EDGE",EDGE,{"disambiguationData":[OSD([sQuery(id+"F0.wireOp",EDGE,"E5")])],"isStart":false}),"instanceName":"1"}),"instanceName":"1"});
            var Q15;
            {var subQ0=sQuery(id+"F0.wireOp",EDGE,"E2");var subQ1=makeQuery(id+"F0.imprint","IMPRINT",EDGE,{"disambiguationData":[TD([[makeQuery(id+"F0.imprint","INTERSECT",VERTEX,{"derivedFrom":[sQuery(id+"F0.wireOp",EDGE,"E0"),subQ0]}),1.0]])],"derivedFrom":subQ0});Q15=makeQuery(id+"F11.opBoolean","MERGE",EDGE,{"derivedFrom":[makeQuery(id+"F9.opPattern","COPY",EDGE,{"derivedFrom":makeQuery(id+"F1.opExtrude","CAP_EDGE",EDGE,{"disambiguationData":[OSD([subQ0]),TDD([subQ1])],"isStart":true}),"instanceName":"1"}),makeQuery(id+"F9.opPattern","COPY",EDGE,{"derivedFrom":makeQuery(id+"F6.opPattern","COPY",EDGE,{"derivedFrom":makeQuery(id+"F1.opExtrude","CAP_EDGE",EDGE,{"disambiguationData":[OSD([subQ0]),TDD([subQ1])],"isStart":false}),"instanceName":"1"}),"instanceName":"1"})]});}
            fillet(context, id + "F14", {"entities" : qUnion([Q0, Q1, Q2, Q3, Q4, Q5, Q6, Q7, Q8, Q9, Q10, Q11, Q12, Q13, Q14, Q15]), "radius" : .5 * mm, "tangentPropagation" : true, "allowEdgeOverflow" : false});
        }
    });
